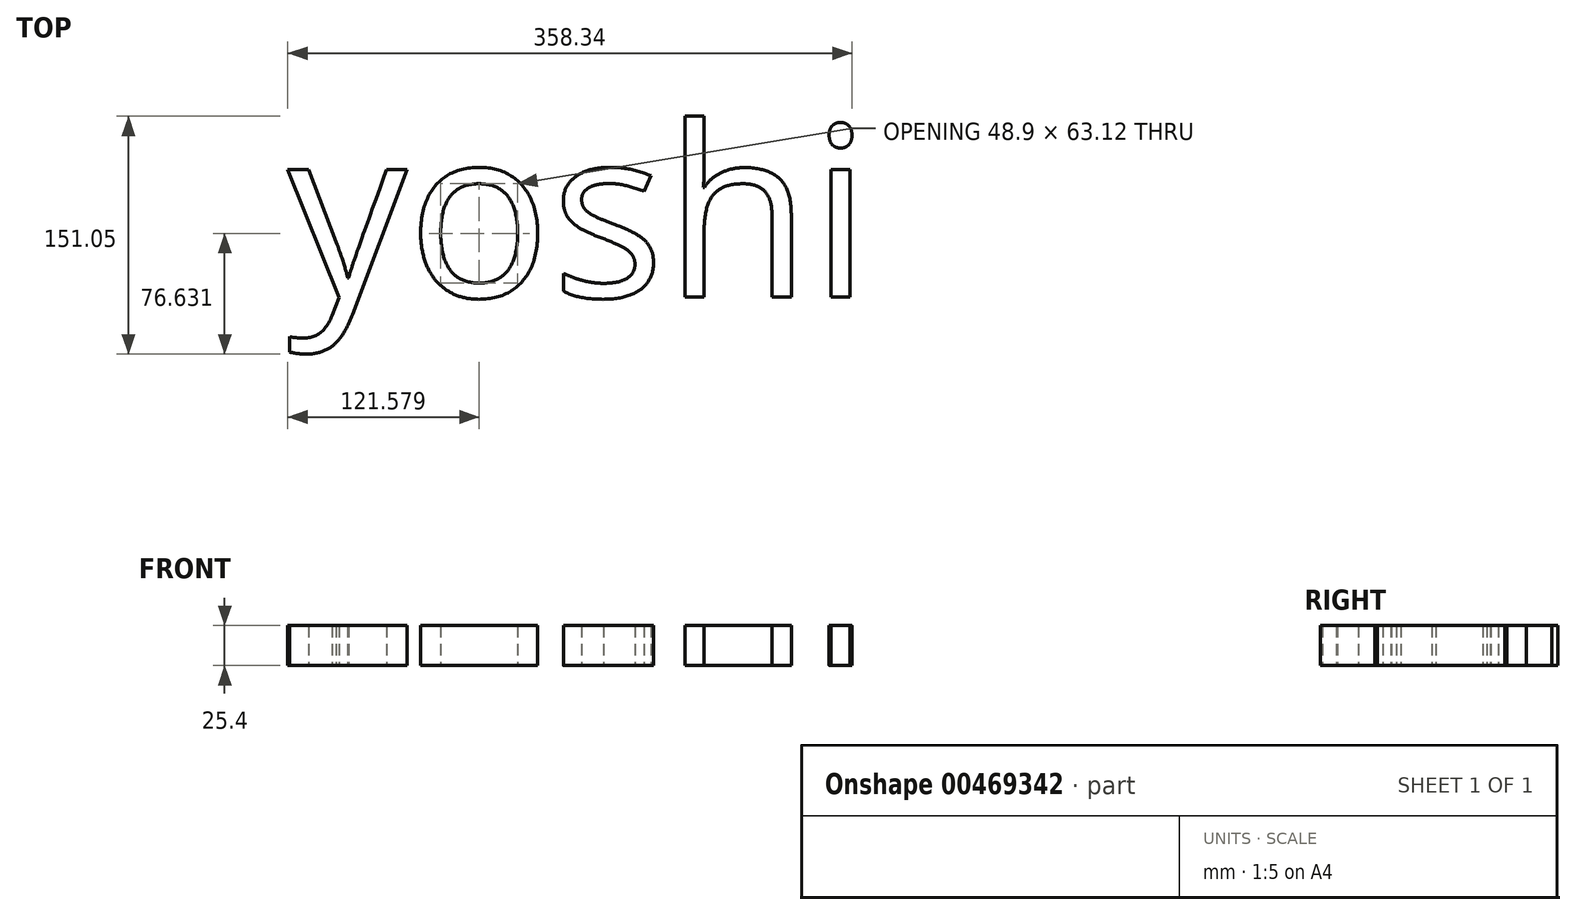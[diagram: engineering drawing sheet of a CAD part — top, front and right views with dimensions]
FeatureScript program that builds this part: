
annotation { "Feature Type Name" : "Feature", "Feature Type Description" : "" }
export const myFeature = defineFeature(function(context is Context, id is Id, definition is map)
    precondition{}
    {
        {
            var Q0;
            Q0=qCreatedBy(makeId("Top.planeOp"),FACE);
            var sketch = newSketch(context, id + "F0", { "sketchPlane" : qUnion([Q0])});
            skText(sketch, "E0", { "text": "yoshi", "fontName": "OpenSans-Regular.ttf"});
            const initialGuessF0  = {"E0": [-0.12075, -0.06994, 1, 0, 0.10874]};
            skSetInitialGuess(sketch, initialGuessF0);
            skSolve(sketch);
        }
        {
            var Q0;
            Q0 = qSketchRegion(id + "F0", true);
            extrude(context, id + "F1", {"entities" : qUnion([Q0]), "depth" : 25.4 * mm});
        }
    });
